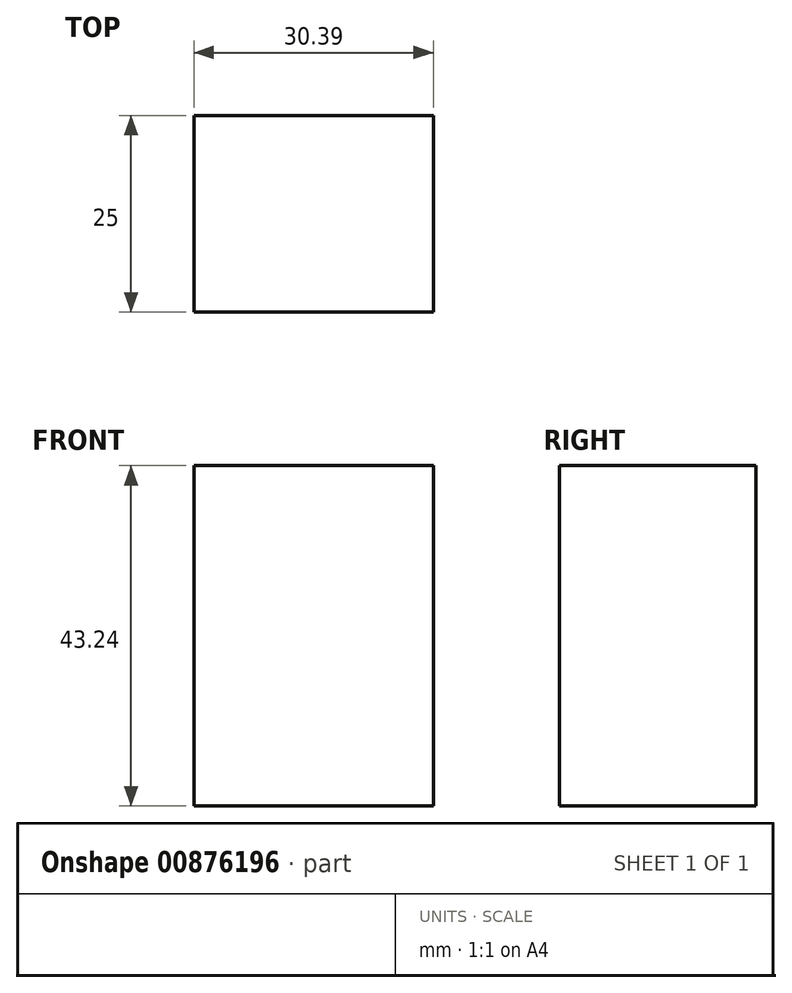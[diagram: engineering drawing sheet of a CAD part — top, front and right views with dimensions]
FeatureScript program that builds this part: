
annotation { "Feature Type Name" : "Feature", "Feature Type Description" : "" }
export const myFeature = defineFeature(function(context is Context, id is Id, definition is map)
    precondition{}
    {
        {
            var Q0;
            Q0=qCreatedBy(makeId("Front.planeOp"),FACE);
            var sketch = newSketch(context, id + "F0", { "sketchPlane" : qUnion([Q0])});
            skLineSegment(sketch, "E0.bottom", {"start": v(-164.1, -19.46) * mm, "end": v(-133.7, -19.46) * mm});
            skLineSegment(sketch, "E0.top", {"start": v(-164.1, -62.7) * mm, "end": v(-133.7, -62.7) * mm});
            skLineSegment(sketch, "E0.left", {"start": v(-164.1, -19.46) * mm, "end": v(-164.1, -62.7) * mm});
            skLineSegment(sketch, "E0.right", {"start": v(-133.7, -19.46) * mm, "end": v(-133.7, -62.7) * mm});
            skSolve(sketch);
        }
        {
            var Q0;
            Q0 = qSketchRegion(id + "F0", true);
            extrude(context, id + "F1", {"entities" : qUnion([Q0]), "depth" : 25 * mm, "offsetDistance" : 25 * mm});
        }
    });
